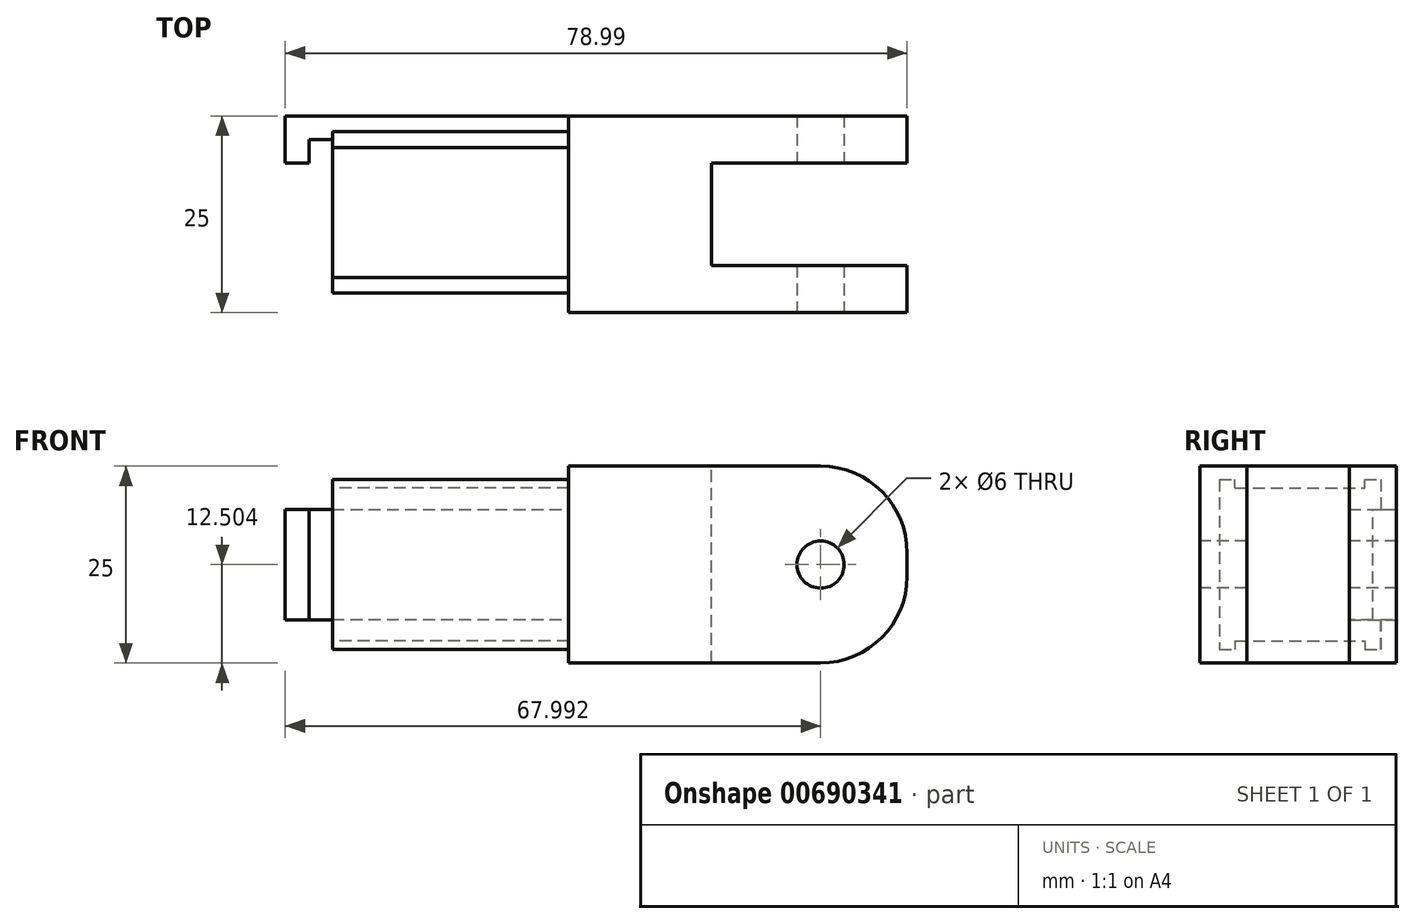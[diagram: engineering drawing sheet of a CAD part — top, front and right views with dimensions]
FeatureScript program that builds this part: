
annotation { "Feature Type Name" : "Feature", "Feature Type Description" : "" }
export const myFeature = defineFeature(function(context is Context, id is Id, definition is map)
    precondition{}
    {
        {
            var Q0;
            Q0=qCreatedBy(makeId("Front.planeOp"),FACE);
            var sketch = newSketch(context, id + "F0", { "sketchPlane" : qUnion([Q0])});
            skLineSegment(sketch, "E0.bottom", {"start": v(-33.78, 14.13) * mm, "end": v(39.22, 14.13) * mm});
            skLineSegment(sketch, "E0.top", {"start": v(-33.78, -10.87) * mm, "end": v(39.22, -10.87) * mm});
            skLineSegment(sketch, "E0.left", {"start": v(-33.78, 14.13) * mm, "end": v(-33.78, -10.87) * mm});
            skLineSegment(sketch, "E0.right", {"start": v(39.22, 14.13) * mm, "end": v(39.22, -10.87) * mm});
            skSolve(sketch);
        }
        {
            var Q0;
            Q0 = qSketchRegion(id + "F0", true);
            extrude(context, id + "F1", {"entities" : qUnion([Q0]), "depth" : 25 * mm, "offsetDistance" : 25 * mm});
        }
        {
            var Q0;
            Q0=makeQuery(id+"F1.opExtrude","CAP_FACE",FACE,{"disambiguationData":[OSD([sQuery(id+"F0.wireOp",EDGE,"E0.bottom"),sQuery(id+"F0.wireOp",EDGE,"E0.top"),sQuery(id+"F0.wireOp",EDGE,"E0.left"),sQuery(id+"F0.wireOp",EDGE,"E0.right")])],"isStart":false});
            var sketch = newSketch(context, id + "F2", { "sketchPlane" : qUnion([Q0])});
            skCircle(sketch, "E1", {"center": v(28.22, 1.63) * mm, "radius": 3 * mm});
            skSolve(sketch);
        }
        {
            var Q0;
            Q0=makeQuery(id+"F2.imprint","IMPRINT",FACE,{"disambiguationData":[TD([[makeQuery(id+"F2.imprint","IMPRINT",EDGE,{"derivedFrom":sQuery(id+"F2.wireOp",EDGE,"E1")}),1.0]])]});
            var Q1;
            Q1=sQuery(id+"F2.wireOp",EDGE,"E1");
            extrude(context, id + "F3", {"entities" : qUnion([Q0]), "operationType" : NewBodyOperationType.REMOVE, "surfaceEntities" : qUnion([Q1]), "endBound" : BoundingType.THROUGH_ALL, "oppositeDirection" : true, "depth" : 30 * mm, "offsetDistance" : 25 * mm});
        }
        {
            var Q0;
            Q0=makeQuery(id+"F1.opExtrude","SWEPT_EDGE",EDGE,{"disambiguationData":[OSD([sQuery(id+"F0.wireOp",EDGE,"E0.bottom"),sQuery(id+"F0.wireOp",EDGE,"E0.right")])]});
            var Q1;
            Q1=makeQuery(id+"F1.opExtrude","SWEPT_EDGE",EDGE,{"disambiguationData":[OSD([sQuery(id+"F0.wireOp",EDGE,"E0.top"),sQuery(id+"F0.wireOp",EDGE,"E0.right")])]});
            fillet(context, id + "F4", {"entities" : qUnion([Q0, Q1]), "radius" : 11 * mm, "tangentPropagation" : true, "allowEdgeOverflow" : false});
        }
        {
            var Q0;
            Q0=qCreatedBy(makeId("Front.planeOp"),FACE);
            cPlane(context, id + "F5", {"entities" : qUnion([Q0]), "cplaneType" : CPlaneType.OFFSET, "offset" : 12.5 * mm, "width" : 150 * mm, "height" : 150 * mm});
        }
        {
            var Q0;
            Q0=qCreatedBy(id+"F5.planeOp",FACE);
            var sketch = newSketch(context, id + "F6", { "sketchPlane" : qUnion([Q0])});
            skLineSegment(sketch, "E2.bottom", {"start": v(39.35, -10.9) * mm, "end": v(14.35, -10.9) * mm});
            skLineSegment(sketch, "E2.top", {"start": v(39.35, 14.77) * mm, "end": v(14.35, 14.77) * mm});
            skLineSegment(sketch, "E2.left", {"start": v(39.35, -10.9) * mm, "end": v(39.35, 14.77) * mm});
            skLineSegment(sketch, "E2.right", {"start": v(14.35, -10.9) * mm, "end": v(14.35, 14.77) * mm});
            skSolve(sketch);
        }
        {
            var Q0;
            Q0=makeQuery(id+"F6.imprint","IMPRINT",FACE,{"disambiguationData":[TD([[makeQuery(id+"F6.imprint","IMPRINT",EDGE,{"derivedFrom":sQuery(id+"F6.wireOp",EDGE,"E2.bottom")}),-1.0]])]});
            extrude(context, id + "F7", {"entities" : qUnion([Q0]), "operationType" : NewBodyOperationType.REMOVE, "endBound" : BoundingType.SYMMETRIC, "oppositeDirection" : true, "depth" : 13 * mm, "offsetDistance" : 25 * mm});
        }
        {
            var Q0;
            Q0=makeQuery(id+"F1.opExtrude","CAP_FACE",FACE,{"disambiguationData":[OSD([sQuery(id+"F0.wireOp",EDGE,"E0.bottom"),sQuery(id+"F0.wireOp",EDGE,"E0.top"),sQuery(id+"F0.wireOp",EDGE,"E0.left"),sQuery(id+"F0.wireOp",EDGE,"E0.right")])],"isStart":false});
            var sketch = newSketch(context, id + "F8", { "sketchPlane" : qUnion([Q0])});
            skLineSegment(sketch, "E3.bottom", {"start": v(-33.78, 14.13) * mm, "end": v(-3.78, 14.13) * mm});
            skLineSegment(sketch, "E3.top", {"start": v(-33.78, -10.87) * mm, "end": v(-3.78, -10.87) * mm});
            skLineSegment(sketch, "E3.left", {"start": v(-33.78, 14.13) * mm, "end": v(-33.78, -10.87) * mm});
            skLineSegment(sketch, "E3.right", {"start": v(-3.78, 14.13) * mm, "end": v(-3.78, -10.87) * mm});
            skSolve(sketch);
        }
        {
            var Q0;
            Q0=makeQuery(id+"F8.imprint","IMPRINT",FACE,{"disambiguationData":[TD([[makeQuery(id+"F8.imprint","IMPRINT",EDGE,{"derivedFrom":sQuery(id+"F8.wireOp",EDGE,"E3.bottom")}),-1.0]])]});
            extrude(context, id + "F9", {"entities" : qUnion([Q0]), "operationType" : NewBodyOperationType.REMOVE, "oppositeDirection" : true, "depth" : 2.5 * mm, "offsetDistance" : 25 * mm});
        }
        {
            var Q0;
            Q0=makeQuery(id+"F1.opExtrude","SWEPT_FACE",FACE,{"disambiguationData":[OSD([sQuery(id+"F0.wireOp",EDGE,"E0.bottom")])]});
            var sketch = newSketch(context, id + "F10", { "sketchPlane" : qUnion([Q0])});
            skLineSegment(sketch, "E4.bottom", {"start": v(-33.78, -22.5) * mm, "end": v(-3.78, -22.5) * mm});
            skLineSegment(sketch, "E4.top", {"start": v(-33.78, 0) * mm, "end": v(-3.78, 0) * mm});
            skLineSegment(sketch, "E4.left", {"start": v(-33.78, -22.5) * mm, "end": v(-33.78, 0) * mm});
            skLineSegment(sketch, "E4.right", {"start": v(-3.78, -22.5) * mm, "end": v(-3.78, 0) * mm});
            skSolve(sketch);
        }
        {
            var Q0;
            Q0=makeQuery(id+"F10.imprint","IMPRINT",FACE,{"disambiguationData":[TD([[makeQuery(id+"F10.imprint","IMPRINT",EDGE,{"derivedFrom":sQuery(id+"F10.wireOp",EDGE,"E4.bottom")}),1.0]])]});
            extrude(context, id + "F11", {"entities" : qUnion([Q0]), "operationType" : NewBodyOperationType.REMOVE, "oppositeDirection" : true, "depth" : 1.7 * mm, "offsetDistance" : 25 * mm});
        }
        {
            var Q0;
            Q0=makeQuery(id+"F1.opExtrude","SWEPT_FACE",FACE,{"disambiguationData":[OSD([sQuery(id+"F0.wireOp",EDGE,"E0.top")])]});
            var sketch = newSketch(context, id + "F12", { "sketchPlane" : qUnion([Q0])});
            skLineSegment(sketch, "E5.bottom", {"start": v(-33.78, 22.5) * mm, "end": v(-3.78, 22.5) * mm});
            skLineSegment(sketch, "E5.top", {"start": v(-33.78, 0) * mm, "end": v(-3.78, 0) * mm});
            skLineSegment(sketch, "E5.left", {"start": v(-33.78, 22.5) * mm, "end": v(-33.78, 0) * mm});
            skLineSegment(sketch, "E5.right", {"start": v(-3.78, 22.5) * mm, "end": v(-3.78, 0) * mm});
            skSolve(sketch);
        }
        {
            var Q0;
            Q0=makeQuery(id+"F12.imprint","IMPRINT",FACE,{"disambiguationData":[TD([[makeQuery(id+"F12.imprint","IMPRINT",EDGE,{"derivedFrom":sQuery(id+"F12.wireOp",EDGE,"E5.bottom")}),-1.0]])]});
            extrude(context, id + "F13", {"entities" : qUnion([Q0]), "operationType" : NewBodyOperationType.REMOVE, "oppositeDirection" : true, "depth" : 1.7 * mm, "offsetDistance" : 25 * mm});
        }
        {
            var Q0;
            Q0=makeQuery(id+"F1.opExtrude","CAP_FACE",FACE,{"disambiguationData":[OSD([sQuery(id+"F0.wireOp",EDGE,"E0.bottom"),sQuery(id+"F0.wireOp",EDGE,"E0.top"),sQuery(id+"F0.wireOp",EDGE,"E0.left"),sQuery(id+"F0.wireOp",EDGE,"E0.right")])],"isStart":true});
            var sketch = newSketch(context, id + "F14", { "sketchPlane" : qUnion([Q0])});
            skLineSegment(sketch, "E6.bottom", {"start": v(33.78, 12.43) * mm, "end": v(3.78, 12.43) * mm});
            skLineSegment(sketch, "E6.top", {"start": v(33.78, 8.63) * mm, "end": v(3.78, 8.63) * mm});
            skLineSegment(sketch, "E6.left", {"start": v(33.78, 12.43) * mm, "end": v(33.78, 8.63) * mm});
            skLineSegment(sketch, "E6.right", {"start": v(3.78, 12.43) * mm, "end": v(3.78, 8.63) * mm});
            skSolve(sketch);
        }
        {
            var Q0;
            Q0=makeQuery(id+"F14.imprint","IMPRINT",FACE,{"disambiguationData":[TD([[makeQuery(id+"F14.imprint","IMPRINT",EDGE,{"derivedFrom":sQuery(id+"F14.wireOp",EDGE,"E6.bottom")}),1.0]])]});
            extrude(context, id + "F15", {"entities" : qUnion([Q0]), "operationType" : NewBodyOperationType.REMOVE, "oppositeDirection" : true, "depth" : 2 * mm, "offsetDistance" : 25 * mm});
        }
        {
            var Q0;
            Q0=makeQuery(id+"F1.opExtrude","CAP_FACE",FACE,{"disambiguationData":[OSD([sQuery(id+"F0.wireOp",EDGE,"E0.bottom"),sQuery(id+"F0.wireOp",EDGE,"E0.top"),sQuery(id+"F0.wireOp",EDGE,"E0.left"),sQuery(id+"F0.wireOp",EDGE,"E0.right")])],"isStart":true});
            var sketch = newSketch(context, id + "F16", { "sketchPlane" : qUnion([Q0])});
            skLineSegment(sketch, "E7.bottom", {"start": v(33.78, -9.17) * mm, "end": v(3.78, -9.17) * mm});
            skLineSegment(sketch, "E7.top", {"start": v(33.78, -5.37) * mm, "end": v(3.78, -5.37) * mm});
            skLineSegment(sketch, "E7.left", {"start": v(33.78, -9.17) * mm, "end": v(33.78, -5.37) * mm});
            skLineSegment(sketch, "E7.right", {"start": v(3.78, -9.17) * mm, "end": v(3.78, -5.37) * mm});
            skSolve(sketch);
        }
        {
            var Q0;
            Q0=makeQuery(id+"F16.imprint","IMPRINT",FACE,{"disambiguationData":[TD([[makeQuery(id+"F16.imprint","IMPRINT",EDGE,{"derivedFrom":sQuery(id+"F16.wireOp",EDGE,"E7.bottom")}),-1.0]])]});
            extrude(context, id + "F17", {"entities" : qUnion([Q0]), "operationType" : NewBodyOperationType.REMOVE, "oppositeDirection" : true, "depth" : 2 * mm, "offsetDistance" : 25 * mm});
        }
        {
            var Q0;
            Q0=makeQuery(id+"F11.boolean.opBoolean","COPY",FACE,{"derivedFrom":makeQuery(id+"F11.opExtrude","CAP_FACE",FACE,{"disambiguationData":[OSD([sQuery(id+"F10.wireOp",EDGE,"E4.bottom"),sQuery(id+"F10.wireOp",EDGE,"E4.top"),sQuery(id+"F10.wireOp",EDGE,"E4.left"),sQuery(id+"F10.wireOp",EDGE,"E4.right")])],"isStart":false})});
            var sketch = newSketch(context, id + "F18", { "sketchPlane" : qUnion([Q0])});
            skLineSegment(sketch, "E8.bottom", {"start": v(-3.78, -20.53) * mm, "end": v(-33.78, -20.53) * mm});
            skLineSegment(sketch, "E8.top", {"start": v(-3.78, -4.03) * mm, "end": v(-33.78, -4.03) * mm});
            skLineSegment(sketch, "E8.left", {"start": v(-3.78, -20.53) * mm, "end": v(-3.78, -4.03) * mm});
            skLineSegment(sketch, "E8.right", {"start": v(-33.78, -20.53) * mm, "end": v(-33.78, -4.03) * mm});
            skSolve(sketch);
        }
        {
            var Q0;
            Q0=makeQuery(id+"F18.imprint","IMPRINT",FACE,{"disambiguationData":[TD([[makeQuery(id+"F18.imprint","IMPRINT",EDGE,{"derivedFrom":sQuery(id+"F18.wireOp",EDGE,"E8.bottom")}),-1.0]])]});
            extrude(context, id + "F19", {"entities" : qUnion([Q0]), "operationType" : NewBodyOperationType.REMOVE, "oppositeDirection" : true, "depth" : 1.1 * mm, "offsetDistance" : 25 * mm});
        }
        {
            var Q0;
            Q0=makeQuery(id+"F13.boolean.opBoolean","COPY",FACE,{"derivedFrom":makeQuery(id+"F13.opExtrude","CAP_FACE",FACE,{"disambiguationData":[OSD([sQuery(id+"F12.wireOp",EDGE,"E5.bottom"),sQuery(id+"F12.wireOp",EDGE,"E5.top"),sQuery(id+"F12.wireOp",EDGE,"E5.left"),sQuery(id+"F12.wireOp",EDGE,"E5.right")])],"isStart":false})});
            var sketch = newSketch(context, id + "F20", { "sketchPlane" : qUnion([Q0])});
            skLineSegment(sketch, "E9.bottom", {"start": v(-3.78, 20.5) * mm, "end": v(-33.78, 20.5) * mm});
            skLineSegment(sketch, "E9.top", {"start": v(-3.78, 4) * mm, "end": v(-33.78, 4) * mm});
            skLineSegment(sketch, "E9.left", {"start": v(-3.78, 20.5) * mm, "end": v(-3.78, 4) * mm});
            skLineSegment(sketch, "E9.right", {"start": v(-33.78, 20.5) * mm, "end": v(-33.78, 4) * mm});
            skSolve(sketch);
        }
        {
            var Q0;
            Q0=makeQuery(id+"F20.imprint","IMPRINT",FACE,{"disambiguationData":[TD([[makeQuery(id+"F20.imprint","IMPRINT",EDGE,{"derivedFrom":sQuery(id+"F20.wireOp",EDGE,"E9.bottom")}),1.0]])]});
            extrude(context, id + "F21", {"entities" : qUnion([Q0]), "operationType" : NewBodyOperationType.REMOVE, "oppositeDirection" : true, "depth" : 1.1 * mm, "offsetDistance" : 25 * mm});
        }
        {
            var Q0;
            Q0=qCreatedBy(makeId("Front.planeOp"),FACE);
            var sketch = newSketch(context, id + "F22", { "sketchPlane" : qUnion([Q0])});
            skLineSegment(sketch, "E10.bottom", {"start": v(-33.77, 8.63) * mm, "end": v(-39.77, 8.63) * mm});
            skLineSegment(sketch, "E10.top", {"start": v(-33.77, -5.37) * mm, "end": v(-39.77, -5.37) * mm});
            skLineSegment(sketch, "E10.left", {"start": v(-33.77, 8.63) * mm, "end": v(-33.77, -5.37) * mm});
            skLineSegment(sketch, "E10.right", {"start": v(-39.77, 8.63) * mm, "end": v(-39.77, -5.37) * mm});
            skSolve(sketch);
        }
        {
            var Q0;
            Q0=makeQuery(id+"F22.imprint","IMPRINT",FACE,{"disambiguationData":[TD([[makeQuery(id+"F22.imprint","IMPRINT",EDGE,{"derivedFrom":sQuery(id+"F22.wireOp",EDGE,"E10.bottom")}),1.0]])]});
            extrude(context, id + "F23", {"entities" : qUnion([Q0]), "operationType" : NewBodyOperationType.ADD, "depth" : 6 * mm, "offsetDistance" : 25 * mm});
        }
        {
            var Q0;
            Q0=makeQuery(id+"F23.opExtrude","SWEPT_FACE",FACE,{"disambiguationData":[OSD([sQuery(id+"F22.wireOp",EDGE,"E10.bottom")])]});
            var sketch = newSketch(context, id + "F24", { "sketchPlane" : qUnion([Q0])});
            skLineSegment(sketch, "E11.bottom", {"start": v(-33.78, -6) * mm, "end": v(-36.78, -6) * mm});
            skLineSegment(sketch, "E11.top", {"start": v(-33.78, -3) * mm, "end": v(-36.78, -3) * mm});
            skLineSegment(sketch, "E11.left", {"start": v(-33.78, -6) * mm, "end": v(-33.78, -3) * mm});
            skLineSegment(sketch, "E11.right", {"start": v(-36.78, -6) * mm, "end": v(-36.78, -3) * mm});
            skSolve(sketch);
        }
        {
            var Q0;
            Q0=makeQuery(id+"F24.imprint","IMPRINT",FACE,{"disambiguationData":[TD([[makeQuery(id+"F24.imprint","IMPRINT",EDGE,{"derivedFrom":sQuery(id+"F24.wireOp",EDGE,"E11.bottom")}),-1.0]])]});
            extrude(context, id + "F25", {"entities" : qUnion([Q0]), "operationType" : NewBodyOperationType.REMOVE, "oppositeDirection" : true, "depth" : 25 * mm, "offsetDistance" : 25 * mm});
        }
    });
